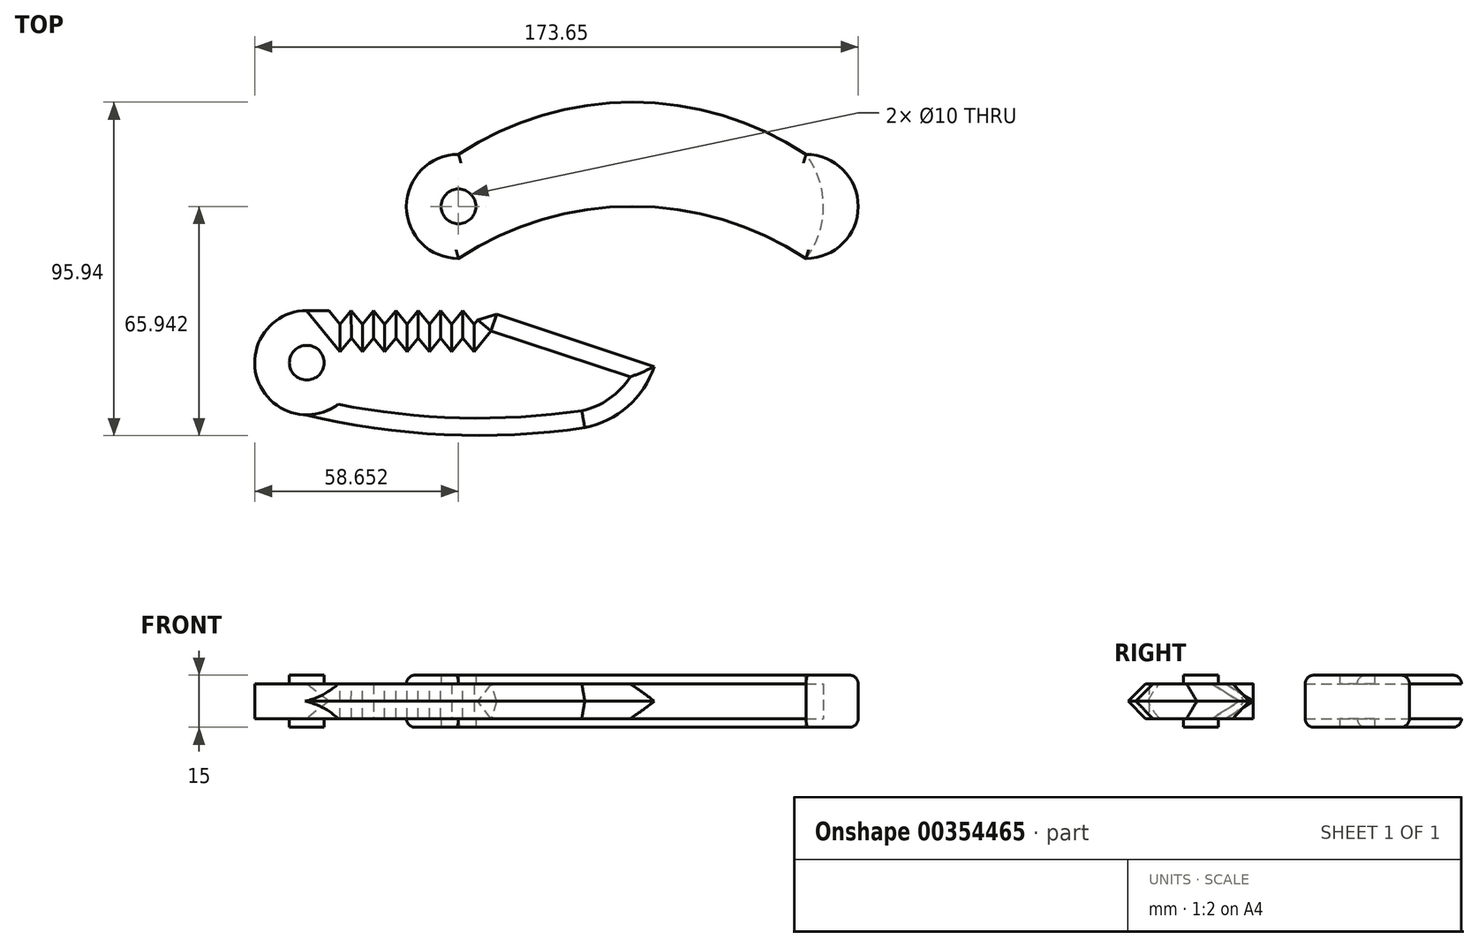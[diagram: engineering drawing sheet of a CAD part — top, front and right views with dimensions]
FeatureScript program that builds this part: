
annotation { "Feature Type Name" : "Feature", "Feature Type Description" : "" }
export const myFeature = defineFeature(function(context is Context, id is Id, definition is map)
    precondition{}
    {
        {
            var Q0;
            Q0=qCreatedBy(makeId("Top.planeOp"),FACE);
            var sketch = newSketch(context, id + "F0", { "sketchPlane" : qUnion([Q0])});
            skPoint(sketch, "E0", {"position": v(-133.45, 64.15) * mm});
            skPoint(sketch, "E1", {"position": v(-33.45, 64.15) * mm});
            skPoint(sketch, "E2", {"position": v(-83.45, 79.15) * mm});
            skArc(sketch, "E3", {"start": v(-133.45, 79.15) * mm, "mid": v(-148.45, 64.15) * mm, "end": v(-133.45, 49.15) * mm});
            skArc(sketch, "E4", {"start": v(-33.45, 49.15) * mm, "mid": v(-18.45, 64.15) * mm, "end": v(-33.45, 79.15) * mm});
            skArc(sketch, "E5", {"start": v(-33.45, 79.15) * mm, "mid": v(-83.45, 94.15) * mm, "end": v(-133.45, 79.15) * mm});
            skArc(sketch, "E6", {"start": v(-33.45, 49.15) * mm, "mid": v(-83.45, 64.15) * mm, "end": v(-133.45, 49.15) * mm});
            skPoint(sketch, "E7", {"position": v(-97.1, 0.42) * mm});
            skArc(sketch, "E8", {"start": v(-97.1, 0.42) * mm, "mid": v(-84.76, 6.58) * mm, "end": v(-77.1, 18.05) * mm});
            skArc(sketch, "E9", {"start": v(-177.6, 4.18) * mm, "mid": v(-137.53, -1.56) * mm, "end": v(-97.1, 0.42) * mm});
            skPoint(sketch, "E10", {"position": v(-125.8, 34.17) * mm});
            skLineSegment(sketch, "E11", {"start": v(-125.8, 34.17) * mm, "end": v(-77.1, 18.05) * mm});
            skPoint(sketch, "E12", {"position": v(-151.47, 34.17) * mm});
            skArc(sketch, "E13", {"start": v(-177.13, 34.17) * mm, "mid": v(-192.1, 19.4) * mm, "end": v(-177.6, 4.18) * mm});
            skPoint(sketch, "E14", {"position": v(-164.3, 34.17) * mm});
            skPoint(sketch, "E15", {"position": v(-138.64, 34.17) * mm});
            skPoint(sketch, "E16", {"position": v(-170.72, 34.17) * mm});
            skPoint(sketch, "E17", {"position": v(-157.88, 34.17) * mm});
            skPoint(sketch, "E18", {"position": v(-145.05, 34.17) * mm});
            skPoint(sketch, "E19", {"position": v(-132.22, 34.17) * mm});
            skPoint(sketch, "E20", {"position": v(-167.5, 30.24) * mm});
            skPoint(sketch, "E21", {"position": v(-161.09, 30.24) * mm});
            skPoint(sketch, "E22", {"position": v(-154.67, 30.25) * mm});
            skPoint(sketch, "E23", {"position": v(-148.25, 30.23) * mm});
            skPoint(sketch, "E24", {"position": v(-141.82, 30.24) * mm});
            skPoint(sketch, "E25", {"position": v(-135.42, 30.22) * mm});
            skPoint(sketch, "E26", {"position": v(-128.98, 30.24) * mm});
            skLineSegment(sketch, "E27", {"start": v(-170.72, 34.17) * mm, "end": v(-167.5, 30.24) * mm});
            skLineSegment(sketch, "E28", {"start": v(-167.5, 30.24) * mm, "end": v(-164.3, 34.17) * mm});
            skLineSegment(sketch, "E29", {"start": v(-164.3, 34.17) * mm, "end": v(-161.09, 30.24) * mm});
            skLineSegment(sketch, "E30", {"start": v(-161.09, 30.24) * mm, "end": v(-157.88, 34.17) * mm});
            skLineSegment(sketch, "E31", {"start": v(-151.47, 34.17) * mm, "end": v(-154.67, 30.25) * mm});
            skLineSegment(sketch, "E32", {"start": v(-145.05, 34.17) * mm, "end": v(-148.25, 30.23) * mm});
            skLineSegment(sketch, "E33", {"start": v(-138.64, 34.17) * mm, "end": v(-141.82, 30.24) * mm});
            skLineSegment(sketch, "E34", {"start": v(-132.22, 34.17) * mm, "end": v(-135.42, 30.22) * mm});
            skLineSegment(sketch, "E35", {"start": v(-128.98, 30.24) * mm, "end": v(-125.73, 34.17) * mm});
            skLineSegment(sketch, "E36", {"start": v(-128.98, 30.24) * mm, "end": v(-132.22, 34.17) * mm});
            skLineSegment(sketch, "E37", {"start": v(-138.64, 34.17) * mm, "end": v(-135.42, 30.22) * mm});
            skLineSegment(sketch, "E38", {"start": v(-141.82, 30.24) * mm, "end": v(-145.05, 34.17) * mm});
            skLineSegment(sketch, "E39", {"start": v(-148.25, 30.23) * mm, "end": v(-151.47, 34.17) * mm});
            skLineSegment(sketch, "E40", {"start": v(-154.67, 30.25) * mm, "end": v(-157.88, 34.17) * mm});
            skLineSegment(sketch, "E41", {"start": v(-177.13, 34.17) * mm, "end": v(-170.72, 34.17) * mm});
            skLineSegment(sketch, "E42", {"start": v(-177.1, 19.17) * mm, "end": v(-177.1, 18.05) * mm});
            skCircle(sketch, "E43", {"center": v(-133.45, 64.15) * mm, "radius": 5 * mm});
            skCircle(sketch, "E44", {"center": v(-177.1, 19.17) * mm, "radius": 5 * mm});
            skArc(sketch, "E45", {"start": v(-33.45, 49.15) * mm, "mid": v(-28.43, 64.15) * mm, "end": v(-33.45, 79.15) * mm});
            skSolve(sketch);
        }
        {
            var Q0;
            {var subQ0=sQuery(id+"F0.wireOp",EDGE,"E8");Q0=makeQuery(id+"F0.imprint","IMPRINT",FACE,{"disambiguationData":[TD([[makeQuery(id+"F0.imprint","IMPRINT",EDGE,{"derivedFrom":subQ0}),1.0]])]});}
            extrude(context, id + "F1", {"entities" : qUnion([Q0]), "depth" : 5 * mm, "hasSecondDirection" : true, "secondDirectionOppositeDirection" : true, "secondDirectionDepth" : 5 * mm});
        }
        {
            var Q0;
            Q0=makeQuery(id+"F0.imprint","IMPRINT",FACE,{"disambiguationData":[TD([[makeQuery(id+"F0.imprint","IMPRINT",EDGE,{"derivedFrom":sQuery(id+"F0.wireOp",EDGE,"E44")}),1.0]])]});
            extrude(context, id + "F2", {"entities" : qUnion([Q0]), "operationType" : NewBodyOperationType.ADD, "depth" : 7.5 * mm, "hasSecondDirection" : true, "secondDirectionOppositeDirection" : true, "secondDirectionDepth" : 7.5 * mm});
        }
        {
            var Q0;
            Q0=makeQuery(id+"F0.imprint","IMPRINT",FACE,{"disambiguationData":[TD([[makeQuery(id+"F0.imprint","IMPRINT",EDGE,{"derivedFrom":sQuery(id+"F0.wireOp",EDGE,"E3")}),1.0]])]});
            var Q1;
            Q1=makeQuery(id+"F0.imprint","IMPRINT",FACE,{"disambiguationData":[TD([[makeQuery(id+"F0.imprint","IMPRINT",EDGE,{"derivedFrom":sQuery(id+"F0.wireOp",EDGE,"E4")}),1.0]])]});
            extrude(context, id + "F3", {"entities" : qUnion([Q0, Q1]), "depth" : 7.5 * mm, "hasSecondDirection" : true, "secondDirectionOppositeDirection" : true, "secondDirectionDepth" : 7.5 * mm});
        }
        {
            var Q0;
            Q0=makeQuery(id+"F0.imprint","IMPRINT",FACE,{"disambiguationData":[TD([[makeQuery(id+"F0.imprint","IMPRINT",EDGE,{"derivedFrom":sQuery(id+"F0.wireOp",EDGE,"E3")}),1.0]])]});
            extrude(context, id + "F4", {"entities" : qUnion([Q0]), "operationType" : NewBodyOperationType.REMOVE, "depth" : 5 * mm, "hasSecondDirection" : true, "secondDirectionOppositeDirection" : true, "secondDirectionDepth" : 5 * mm});
        }
        {
            var Q0;
            Q0=makeQuery(id+"F1.opExtrude","CAP_EDGE",EDGE,{"disambiguationData":[OSD([sQuery(id+"F0.wireOp",EDGE,"E8")])],"isStart":false});
            var Q1;
            Q1=makeQuery(id+"F1.opExtrude","CAP_EDGE",EDGE,{"disambiguationData":[OSD([sQuery(id+"F0.wireOp",EDGE,"E8")])],"isStart":true});
            var Q2;
            Q2=makeQuery(id+"F1.opExtrude","CAP_EDGE",EDGE,{"disambiguationData":[OSD([sQuery(id+"F0.wireOp",EDGE,"E9")])],"isStart":false});
            var Q3;
            Q3=makeQuery(id+"F1.opExtrude","CAP_EDGE",EDGE,{"disambiguationData":[OSD([sQuery(id+"F0.wireOp",EDGE,"E9")])],"isStart":true});
            chamfer(context, id + "F5", {"entities" : qUnion([Q0, Q1, Q2, Q3]), "width" : 5 * mm, "tangentPropagation" : true});
        }
        {
            var Q0;
            Q0=makeQuery(id+"F3.opExtrude","CAP_EDGE",EDGE,{"disambiguationData":[OSD([sQuery(id+"F0.wireOp",EDGE,"E5")])],"isStart":true});
            var Q1;
            Q1=makeQuery(id+"F3.opExtrude","CAP_EDGE",EDGE,{"disambiguationData":[OSD([sQuery(id+"F0.wireOp",EDGE,"E4")])],"isStart":true});
            var Q2;
            Q2=makeQuery(id+"F3.opExtrude","CAP_EDGE",EDGE,{"disambiguationData":[OSD([sQuery(id+"F0.wireOp",EDGE,"E6")])],"isStart":true});
            var Q3;
            Q3=makeQuery(id+"F3.opExtrude","CAP_EDGE",EDGE,{"disambiguationData":[OSD([sQuery(id+"F0.wireOp",EDGE,"E3")])],"isStart":true});
            var Q4;
            Q4=makeQuery(id+"F3.opExtrude","CAP_EDGE",EDGE,{"disambiguationData":[OSD([sQuery(id+"F0.wireOp",EDGE,"E3")])],"isStart":false});
            var Q5;
            Q5=makeQuery(id+"F3.opExtrude","CAP_EDGE",EDGE,{"disambiguationData":[OSD([sQuery(id+"F0.wireOp",EDGE,"E5")])],"isStart":false});
            var Q6;
            Q6=makeQuery(id+"F3.opExtrude","CAP_EDGE",EDGE,{"disambiguationData":[OSD([sQuery(id+"F0.wireOp",EDGE,"E4")])],"isStart":false});
            var Q7;
            Q7=makeQuery(id+"F3.opExtrude","CAP_EDGE",EDGE,{"disambiguationData":[OSD([sQuery(id+"F0.wireOp",EDGE,"E6")])],"isStart":false});
            fillet(context, id + "F6", {"entities" : qUnion([Q0, Q1, Q2, Q3, Q4, Q5, Q6, Q7]), "radius" : 2.5 * mm, "tangentPropagation" : true, "allowEdgeOverflow" : false});
        }
        {
            var Q0;
            Q0=makeQuery(id+"F1.opExtrude","CAP_EDGE",EDGE,{"disambiguationData":[OSD([sQuery(id+"F0.wireOp",EDGE,"E28")])],"isStart":false});
            var Q1;
            Q1=makeQuery(id+"F1.opExtrude","CAP_EDGE",EDGE,{"disambiguationData":[OSD([sQuery(id+"F0.wireOp",EDGE,"E27")])],"isStart":false});
            var Q2;
            Q2=makeQuery(id+"F1.opExtrude","CAP_EDGE",EDGE,{"disambiguationData":[OSD([sQuery(id+"F0.wireOp",EDGE,"E29")])],"isStart":false});
            var Q3;
            Q3=makeQuery(id+"F1.opExtrude","CAP_EDGE",EDGE,{"disambiguationData":[OSD([sQuery(id+"F0.wireOp",EDGE,"E30")])],"isStart":false});
            var Q4;
            Q4=makeQuery(id+"F1.opExtrude","CAP_EDGE",EDGE,{"disambiguationData":[OSD([sQuery(id+"F0.wireOp",EDGE,"E40")])],"isStart":false});
            var Q5;
            Q5=makeQuery(id+"F1.opExtrude","CAP_EDGE",EDGE,{"disambiguationData":[OSD([sQuery(id+"F0.wireOp",EDGE,"E31")])],"isStart":false});
            var Q6;
            Q6=makeQuery(id+"F1.opExtrude","CAP_EDGE",EDGE,{"disambiguationData":[OSD([sQuery(id+"F0.wireOp",EDGE,"E39")])],"isStart":false});
            var Q7;
            Q7=makeQuery(id+"F1.opExtrude","CAP_EDGE",EDGE,{"disambiguationData":[OSD([sQuery(id+"F0.wireOp",EDGE,"E32")])],"isStart":false});
            var Q8;
            Q8=makeQuery(id+"F1.opExtrude","CAP_EDGE",EDGE,{"disambiguationData":[OSD([sQuery(id+"F0.wireOp",EDGE,"E38")])],"isStart":false});
            var Q9;
            Q9=makeQuery(id+"F1.opExtrude","CAP_EDGE",EDGE,{"disambiguationData":[OSD([sQuery(id+"F0.wireOp",EDGE,"E33")])],"isStart":false});
            var Q10;
            Q10=makeQuery(id+"F1.opExtrude","CAP_EDGE",EDGE,{"disambiguationData":[OSD([sQuery(id+"F0.wireOp",EDGE,"E37")])],"isStart":false});
            var Q11;
            Q11=makeQuery(id+"F5.opChamfer","BLEND_EDGE",EDGE,{"blendedFrom":[makeQuery(id+"F1.opExtrude","CAP_EDGE",EDGE,{"disambiguationData":[OSD([sQuery(id+"F0.wireOp",EDGE,"E11")])],"isStart":false}),makeQuery(id+"F1.opExtrude","SWEPT_FACE",FACE,{"disambiguationData":[OSD([sQuery(id+"F0.wireOp",EDGE,"E34")])]})],"blendedInto":[makeQuery(id+"F1.opExtrude","SWEPT_FACE",FACE,{"disambiguationData":[OSD([sQuery(id+"F0.wireOp",EDGE,"E34")])]})]});
            var Q12;
            Q12=makeQuery(id+"F5.opChamfer","BLEND_EDGE",EDGE,{"blendedFrom":[makeQuery(id+"F1.opExtrude","CAP_EDGE",EDGE,{"disambiguationData":[OSD([sQuery(id+"F0.wireOp",EDGE,"E11")])],"isStart":false}),makeQuery(id+"F1.opExtrude","SWEPT_FACE",FACE,{"disambiguationData":[OSD([sQuery(id+"F0.wireOp",EDGE,"E36")])]})],"blendedInto":[makeQuery(id+"F1.opExtrude","SWEPT_FACE",FACE,{"disambiguationData":[OSD([sQuery(id+"F0.wireOp",EDGE,"E36")])]})]});
            var Q13;
            Q13=makeQuery(id+"F1.opExtrude","CAP_EDGE",EDGE,{"disambiguationData":[OSD([sQuery(id+"F0.wireOp",EDGE,"E34")])],"isStart":false});
            var Q14;
            Q14=makeQuery(id+"F1.opExtrude","CAP_EDGE",EDGE,{"disambiguationData":[OSD([sQuery(id+"F0.wireOp",EDGE,"E34")])],"isStart":true});
            var Q15;
            Q15=makeQuery(id+"F1.opExtrude","CAP_EDGE",EDGE,{"disambiguationData":[OSD([sQuery(id+"F0.wireOp",EDGE,"E37")])],"isStart":true});
            var Q16;
            Q16=makeQuery(id+"F1.opExtrude","CAP_EDGE",EDGE,{"disambiguationData":[OSD([sQuery(id+"F0.wireOp",EDGE,"E33")])],"isStart":true});
            var Q17;
            Q17=makeQuery(id+"F1.opExtrude","CAP_EDGE",EDGE,{"disambiguationData":[OSD([sQuery(id+"F0.wireOp",EDGE,"E38")])],"isStart":true});
            var Q18;
            Q18=makeQuery(id+"F1.opExtrude","CAP_EDGE",EDGE,{"disambiguationData":[OSD([sQuery(id+"F0.wireOp",EDGE,"E32")])],"isStart":true});
            var Q19;
            Q19=makeQuery(id+"F1.opExtrude","CAP_EDGE",EDGE,{"disambiguationData":[OSD([sQuery(id+"F0.wireOp",EDGE,"E39")])],"isStart":true});
            var Q20;
            Q20=makeQuery(id+"F1.opExtrude","CAP_EDGE",EDGE,{"disambiguationData":[OSD([sQuery(id+"F0.wireOp",EDGE,"E31")])],"isStart":true});
            var Q21;
            Q21=makeQuery(id+"F1.opExtrude","CAP_EDGE",EDGE,{"disambiguationData":[OSD([sQuery(id+"F0.wireOp",EDGE,"E40")])],"isStart":true});
            var Q22;
            Q22=makeQuery(id+"F1.opExtrude","CAP_EDGE",EDGE,{"disambiguationData":[OSD([sQuery(id+"F0.wireOp",EDGE,"E30")])],"isStart":true});
            var Q23;
            Q23=makeQuery(id+"F1.opExtrude","CAP_EDGE",EDGE,{"disambiguationData":[OSD([sQuery(id+"F0.wireOp",EDGE,"E29")])],"isStart":true});
            var Q24;
            Q24=makeQuery(id+"F1.opExtrude","CAP_EDGE",EDGE,{"disambiguationData":[OSD([sQuery(id+"F0.wireOp",EDGE,"E28")])],"isStart":true});
            var Q25;
            Q25=makeQuery(id+"F1.opExtrude","CAP_EDGE",EDGE,{"disambiguationData":[OSD([sQuery(id+"F0.wireOp",EDGE,"E27")])],"isStart":true});
            var Q26;
            Q26=makeQuery(id+"F1.opExtrude","CAP_EDGE",EDGE,{"disambiguationData":[OSD([sQuery(id+"F0.wireOp",EDGE,"E11")])],"isStart":false});
            var Q27;
            Q27=makeQuery(id+"F1.opExtrude","CAP_EDGE",EDGE,{"disambiguationData":[OSD([sQuery(id+"F0.wireOp",EDGE,"E11")])],"isStart":true});
            var Q28;
            Q28=makeQuery(id+"F1.opExtrude","CAP_EDGE",EDGE,{"disambiguationData":[OSD([sQuery(id+"F0.wireOp",EDGE,"E35")])],"isStart":false});
            var Q29;
            Q29=makeQuery(id+"F1.opExtrude","CAP_EDGE",EDGE,{"disambiguationData":[OSD([sQuery(id+"F0.wireOp",EDGE,"E35")])],"isStart":true});
            var Q30;
            Q30=makeQuery(id+"F1.opExtrude","SWEPT_EDGE",EDGE,{"disambiguationData":[OSD([sQuery(id+"F0.wireOp",EDGE,"E11"),sQuery(id+"F0.wireOp",EDGE,"E35")])]});
            var Q31;
            Q31=makeQuery(id+"F1.opExtrude","CAP_EDGE",EDGE,{"disambiguationData":[OSD([sQuery(id+"F0.wireOp",EDGE,"E36")])],"isStart":false});
            var Q32;
            Q32=makeQuery(id+"F1.opExtrude","CAP_EDGE",EDGE,{"disambiguationData":[OSD([sQuery(id+"F0.wireOp",EDGE,"E36")])],"isStart":true});
            chamfer(context, id + "F7", {"entities" : qUnion([Q0, Q1, Q2, Q3, Q4, Q5, Q6, Q7, Q8, Q9, Q10, Q11, Q12, Q13, Q14, Q15, Q16, Q17, Q18, Q19, Q20, Q21, Q22, Q23, Q24, Q25, Q26, Q27, Q28, Q29, Q30, Q31, Q32]), "width" : 5 * mm, "tangentPropagation" : true});
        }
    });
